annotation { "Feature Type Name" : "Feature", "Feature Type Description" : "" }
export const myFeature = defineFeature(function(context is Context, id is Id, definition is map)
    precondition{}
    {
        {
            var Q0;
            Q0=qCreatedBy(makeId("Top.planeOp"),FACE);
            var sketch = newSketch(context, id + "F0", { "sketchPlane" : qUnion([Q0])});
            skCircle(sketch, "E0", {"center": v(0.94, -3) * mm, "radius": 27.74 * mm});
            skPoint(sketch, "E0.first.point", {"position": v(1.58, 24.74) * mm});
            skPoint(sketch, "E0.second.point", {"position": v(0.52, -30.73) * mm});
            skPoint(sketch, "E0.third.point", {"position": v(-26.76, -1.33) * mm});
            skLineSegment(sketch, "E1", {"start": v(-24.87, 7.2) * mm, "end": v(-34.2, 7.2) * mm});
            skLineSegment(sketch, "E2", {"start": v(-34.2, 7.2) * mm, "end": v(-33.08, 3.11) * mm});
            skLineSegment(sketch, "E3", {"start": v(-33.08, 3.11) * mm, "end": v(-35, -2.1) * mm});
            skLineSegment(sketch, "E4", {"start": v(-35, -2.1) * mm, "end": v(-26.8, -2.1) * mm});
            skLineSegment(sketch, "E5", {"start": v(26.78, 7.1) * mm, "end": v(35.71, 7.1) * mm});
            skLineSegment(sketch, "E6", {"start": v(35.71, 7.1) * mm, "end": v(34.66, 3.21) * mm});
            skLineSegment(sketch, "E7", {"start": v(34.66, 3.21) * mm, "end": v(36.55, -2.1) * mm});
            skLineSegment(sketch, "E8", {"start": v(36.55, -2.1) * mm, "end": v(28.67, -2.25) * mm});
            skFitSpline(sketch, "E9", {"points": [v(-6, -4.72) * mm, v(-5.23, -5.35) * mm, v(-3.9, -6.35) * mm, v(-2.48, -6.98) * mm, v(-0.85, -7.35) * mm, v(0.35, -7.37) * mm, v(2.08, -7.15) * mm, v(3.86, -6.6) * mm, v(5.5, -5.84) * mm, v(6.83, -5.05) * mm, v(7.95, -4.34) * mm, v(8.2, -4.17) * mm, v(8.54, -3.89) * mm, v(8.14, -4.78) * mm, v(7.2, -5.82) * mm, v(5.2, -7.28) * mm, v(2.9, -8.45) * mm, v(3.98, -8.47) * mm, v(5.87, -8.12) * mm, v(7.76, -7.26) * mm, v(8.43, -6.75) * mm, v(8.6, -6.46) * mm, v(8.47, -7.15) * mm, v(6.46, -8.4) * mm, v(3.8, -9.28) * mm, v(1.11, -9.42) * mm, v(-0.95, -9.06) * mm], "startDerivative": vector(22.31, -18.25) * mm, "endDerivative": vector(-43, 9.84) * mm});
            skFitSpline(sketch, "E10", {"points": [v(-6, -4.72) * mm, v(-5.19, -6.01) * mm, v(-3.81, -7.48) * mm, v(-3.02, -8.2) * mm, v(-2.26, -9.47) * mm, v(-1.53, -11.45) * mm, v(-1.17, -13.95) * mm, v(-1.2, -16.67) * mm, v(-0.95, -15.45) * mm, v(-0.68, -11.98) * mm, v(-0.91, -9.36) * mm, v(-0.95, -9.06) * mm], "startDerivative": vector(8.3, -15) * mm, "endDerivative": vector(-0.86, 6) * mm});
            skFitSpline(sketch, "E11", {"points": [v(2.34, -9.66) * mm, v(2.02, -10.62) * mm, v(1.67, -12.76) * mm, v(1.67, -14.3) * mm, v(2.06, -16.19) * mm, v(2.36, -16.95) * mm, v(1.82, -16.92) * mm, v(-0.01, -17.17) * mm, v(-1.66, -17.64) * mm, v(-3.97, -18.79) * mm, v(-6.02, -20.44) * mm, v(-6.96, -21.68) * mm, v(-5.91, -20.77) * mm, v(-3.67, -19.33) * mm, v(-1.3, -18.4) * mm, v(0.83, -18.07) * mm, v(2.42, -18.3) * mm, v(3.7, -19.03) * mm, v(4.04, -19.68) * mm, v(3.45, -20.21) * mm, v(1.98, -19.81) * mm, v(1.3, -18.87) * mm, v(1.45, -19.8) * mm, v(2.36, -20.56) * mm, v(3.3, -21.02) * mm, v(4.84, -20.7) * mm, v(5.53, -19.8) * mm, v(6.38, -20.28) * mm, v(7.16, -20.84) * mm, v(8.14, -21.87) * mm, v(7.64, -20.68) * mm, v(6.28, -19.14) * mm, v(4.5, -17.53) * mm, v(3.33, -16.29) * mm, v(2.56, -14.18) * mm, v(2.24, -11.68) * mm, v(2.33, -10.24) * mm, v(2.34, -9.66) * mm]});
            skLineSegment(sketch, "E12", {"start": v(-24.87, 7.2) * mm, "end": v(28.1, 7.1) * mm});
            skLineSegment(sketch, "E13", {"start": v(-27.68, -2.1) * mm, "end": v(29.48, -2.24) * mm});
            skCircle(sketch, "E14.0", {"center": v(0.94, -3) * mm, "radius": 29.33 * mm});
            skCircle(sketch, "E15.0", {"center": v(0.94, -3) * mm, "radius": 31.31 * mm});
            skLineSegment(sketch, "E16.0", {"start": v(-24.87, 6.45) * mm, "end": v(28.1, 6.35) * mm});
            skLineSegment(sketch, "E17.0", {"start": v(-24.87, 6.45) * mm, "end": v(-33.21, 6.45) * mm});
            skLineSegment(sketch, "E18", {"start": v(28.1, 6.35) * mm, "end": v(34.73, 6.35) * mm});
            skLineSegment(sketch, "E19.0", {"start": v(-27.68, -1.35) * mm, "end": v(29.48, -1.49) * mm});
            skLineSegment(sketch, "E20", {"start": v(-27.68, -1.35) * mm, "end": v(-33.91, -1.33) * mm});
            skLineSegment(sketch, "E21", {"start": v(29.48, -1.49) * mm, "end": v(35.54, -1.5) * mm});
            skLineSegment(sketch, "E22.0", {"start": v(34.73, 6.35) * mm, "end": v(33.88, 3.18) * mm});
            skLineSegment(sketch, "E23.0", {"start": v(33.88, 3.18) * mm, "end": v(35.54, -1.5) * mm});
            skLineSegment(sketch, "E24.0", {"start": v(-32.3, 3.08) * mm, "end": v(-33.91, -1.33) * mm});
            skLineSegment(sketch, "E25.trimOffspring", {"start": v(-33.21, 6.45) * mm, "end": v(-32.3, 3.08) * mm});
            skText(sketch, "E26", { "text": "SCIENCE CHALLENGE", "fontName": "OpenSans-Regular.ttf"});
            skText(sketch, "E27", { "text": "GEMINI", "fontName": "OpenSans-Bold.ttf"});
            skText(sketch, "E28", { "text": "VJC", "fontName": "Arimo-Bold.ttf"});
            skLineSegment(sketch, "E29", {"start": v(6.9, 1.33) * mm, "end": v(6.9, 2.22) * mm});
            skLineSegment(sketch, "E30", {"start": v(6.9, 2.22) * mm, "end": v(7.18, 2.22) * mm});
            skLineSegment(sketch, "E31", {"start": v(7.18, 2.22) * mm, "end": v(7.26, 2.22) * mm});
            skLineSegment(sketch, "E32", {"start": v(7.26, 2.22) * mm, "end": v(7.26, 1.34) * mm});
            skLineSegment(sketch, "E33", {"start": v(7.26, 1.34) * mm, "end": v(6.9, 1.33) * mm});
            skCircle(sketch, "E34", {"center": v(1.48, 31.52) * mm, "radius": 3.06 * mm});
            skCircle(sketch, "E35.0", {"center": v(1.48, 31.52) * mm, "radius": 5 * mm});
            skText(sketch, "E36", { "text": "Ad Hoc", "fontName": "AllertaStencil-Regular.ttf"});
            const initialGuessF0  = {"E26": [-0.03136, 0, 1, 0, 0.0047], "E27": [-0.0116, -0.02738, 1, 0, 0.00494], "E28": [-0.01032, 0.01442, 1, 0, 0.00826], "E36": [-0.01374, 0.00786, 1, 0, 0.00598]};
            skSetInitialGuess(sketch, initialGuessF0);
            skSolve(sketch);
        }
        {
            var Q0;
            Q0=makeQuery(id+"F0.imprint","IMPRINT",FACE,{"disambiguationData":[TD([[makeQuery(id+"F0.imprint","IMPRINT",EDGE,{"derivedFrom":sQuery(id+"F0.wireOp",EDGE,"f2c7ee9f-897c-4c1d-89b3-a48ac7c6bfa7.sketch_text.stroke-0")}),1.0]])]});
            var Q1;
            {var subQ0=sQuery(id+"F0.wireOp",EDGE,"E15.0");var subQ1=sQuery(id+"F0.wireOp",EDGE,"E1");var subQ2=makeQuery(id+"F0.imprint","INTERSECT",VERTEX,{"derivedFrom":[subQ1,subQ0]});Q1=makeQuery(id+"F0.imprint","IMPRINT",FACE,{"disambiguationData":[TD([[makeQuery(id+"F0.imprint","IMPRINT",EDGE,{"disambiguationData":[TD([[subQ2,1.0]])],"derivedFrom":subQ1}),-1.0]])]});}
            var Q2;
            Q2=makeQuery(id+"F0.imprint","IMPRINT",FACE,{"disambiguationData":[TD([[makeQuery(id+"F0.imprint","IMPRINT",EDGE,{"derivedFrom":sQuery(id+"F0.wireOp",EDGE,"26462852-2f77-49b2-9a3d-6dfd93b606f1.sketch_text.stroke-0")}),1.0]])]});
            var Q3;
            {var subQ0=sQuery(id+"F0.wireOp",EDGE,"E15.0");var subQ1=sQuery(id+"F0.wireOp",EDGE,"E4");var subQ2=makeQuery(id+"F0.imprint","INTERSECT",VERTEX,{"derivedFrom":[subQ1,subQ0]});Q3=makeQuery(id+"F0.imprint","IMPRINT",FACE,{"disambiguationData":[TD([[makeQuery(id+"F0.imprint","IMPRINT",EDGE,{"disambiguationData":[TD([[subQ2,-1.0]])],"derivedFrom":subQ1}),-1.0]])]});}
            var Q4;
            {var subQ7=sQuery(id+"F0.wireOp",EDGE,"E2");Q4=makeQuery(id+"F0.imprint","IMPRINT",FACE,{"disambiguationData":[TD([[makeQuery(id+"F0.imprint","IMPRINT",EDGE,{"derivedFrom":subQ7}),1.0]])]});}
            var Q5;
            {var subQ3=sQuery(id+"F0.wireOp",EDGE,"E17.0");var subQ10=makeQuery(id+"F0.imprint","IMPRINT",VERTEX,{"derivedFrom":subQ3});Q5=makeQuery(id+"F0.imprint","IMPRINT",FACE,{"disambiguationData":[TD([[makeQuery(id+"F0.imprint","IMPRINT",EDGE,{"disambiguationData":[TD([[subQ10,1.0]])],"derivedFrom":subQ3}),-1.0]])]});}
            var Q6;
            {var subQ0=sQuery(id+"F0.wireOp",EDGE,"E1");var subQ5=sQuery(id+"F0.wireOp",EDGE,"E14.0");var subQ6=makeQuery(id+"F0.imprint","INTERSECT",VERTEX,{"derivedFrom":[subQ0,subQ5]});Q6=makeQuery(id+"F0.imprint","IMPRINT",FACE,{"disambiguationData":[TD([[makeQuery(id+"F0.imprint","IMPRINT",EDGE,{"disambiguationData":[TD([[subQ6,-1.0]])],"derivedFrom":subQ5}),1.0]])]});}
            var Q7;
            {var subQ1=sQuery(id+"F0.wireOp",EDGE,"E5");var subQ6=sQuery(id+"F0.wireOp",EDGE,"E0");var subQ7=makeQuery(id+"F0.imprint","INTERSECT",VERTEX,{"derivedFrom":[subQ6,subQ1]});Q7=makeQuery(id+"F0.imprint","IMPRINT",FACE,{"disambiguationData":[TD([[makeQuery(id+"F0.imprint","IMPRINT",EDGE,{"disambiguationData":[TD([[subQ7,1.0]])],"derivedFrom":subQ6}),-1.0]])]});}
            var Q8;
            {var subQ0=sQuery(id+"F0.wireOp",EDGE,"E15.0");var subQ1=sQuery(id+"F0.wireOp",EDGE,"E5");var subQ2=makeQuery(id+"F0.imprint","INTERSECT",VERTEX,{"derivedFrom":[subQ1,subQ0]});Q8=makeQuery(id+"F0.imprint","IMPRINT",FACE,{"disambiguationData":[TD([[makeQuery(id+"F0.imprint","IMPRINT",EDGE,{"disambiguationData":[TD([[subQ2,1.0]])],"derivedFrom":subQ1}),-1.0]])]});}
            var Q9;
            {var subQ11=sQuery(id+"F0.wireOp",EDGE,"E6");Q9=makeQuery(id+"F0.imprint","IMPRINT",FACE,{"disambiguationData":[TD([[makeQuery(id+"F0.imprint","IMPRINT",EDGE,{"derivedFrom":subQ11}),-1.0]])]});}
            var Q10;
            {var subQ0=sQuery(id+"F0.wireOp",EDGE,"E13");var subQ1=sQuery(id+"F0.wireOp",EDGE,"E0");var subQ2=makeQuery(id+"F0.imprint","INTERSECT",VERTEX,{"disambiguationData":[OD(0.0)],"derivedFrom":[subQ1,subQ0]});Q10=makeQuery(id+"F0.imprint","IMPRINT",FACE,{"disambiguationData":[TD([[makeQuery(id+"F0.imprint","IMPRINT",EDGE,{"disambiguationData":[TD([[subQ2,-1.0]])],"derivedFrom":subQ1}),1.0]])]});}
            var Q11;
            {var subQ0=sQuery(id+"F0.wireOp",EDGE,"E13");var subQ3=sQuery(id+"F0.wireOp",EDGE,"E0");var subQ4=makeQuery(id+"F0.imprint","INTERSECT",VERTEX,{"disambiguationData":[OD(0.0)],"derivedFrom":[subQ3,subQ0]});Q11=makeQuery(id+"F0.imprint","IMPRINT",FACE,{"disambiguationData":[TD([[makeQuery(id+"F0.imprint","IMPRINT",EDGE,{"disambiguationData":[TD([[subQ4,-1.0]])],"derivedFrom":subQ3}),-1.0]])]});}
            var Q12;
            {var subQ0=sQuery(id+"F0.wireOp",EDGE,"E15.0");var subQ1=sQuery(id+"F0.wireOp",EDGE,"E8");var subQ2=makeQuery(id+"F0.imprint","INTERSECT",VERTEX,{"derivedFrom":[subQ1,subQ0]});Q12=makeQuery(id+"F0.imprint","IMPRINT",FACE,{"disambiguationData":[TD([[makeQuery(id+"F0.imprint","IMPRINT",EDGE,{"disambiguationData":[TD([[subQ2,-1.0]])],"derivedFrom":subQ1}),-1.0]])]});}
            var Q13;
            {var subQ0=sQuery(id+"F0.wireOp",EDGE,"E15.0");var subQ1=sQuery(id+"F0.wireOp",EDGE,"E1");var subQ2=makeQuery(id+"F0.imprint","INTERSECT",VERTEX,{"derivedFrom":[subQ1,subQ0]});Q13=makeQuery(id+"F0.imprint","IMPRINT",FACE,{"disambiguationData":[TD([[makeQuery(id+"F0.imprint","IMPRINT",EDGE,{"disambiguationData":[TD([[subQ2,1.0]])],"derivedFrom":subQ1}),1.0]])]});}
            var Q14;
            {var subQ0=sQuery(id+"F0.wireOp",EDGE,"E15.0");var subQ1=sQuery(id+"F0.wireOp",EDGE,"E4");var subQ2=makeQuery(id+"F0.imprint","INTERSECT",VERTEX,{"derivedFrom":[subQ1,subQ0]});Q14=makeQuery(id+"F0.imprint","IMPRINT",FACE,{"disambiguationData":[TD([[makeQuery(id+"F0.imprint","IMPRINT",EDGE,{"disambiguationData":[TD([[subQ2,-1.0]])],"derivedFrom":subQ1}),1.0]])]});}
            var Q15;
            {var subQ0=sQuery(id+"F0.wireOp",EDGE,"E4");var subQ1=sQuery(id+"F0.wireOp",EDGE,"E0");var subQ2=makeQuery(id+"F0.imprint","INTERSECT",VERTEX,{"derivedFrom":[subQ1,subQ0]});Q15=makeQuery(id+"F0.imprint","IMPRINT",FACE,{"disambiguationData":[TD([[makeQuery(id+"F0.imprint","IMPRINT",EDGE,{"disambiguationData":[TD([[subQ2,1.0]])],"derivedFrom":subQ1}),-1.0]])]});}
            var Q16;
            Q16=makeQuery(id+"F0.imprint","IMPRINT",FACE,{"disambiguationData":[TD([[makeQuery(id+"F0.imprint","IMPRINT",EDGE,{"derivedFrom":sQuery(id+"F0.wireOp",EDGE,"E9")}),1.0]])]});
            var Q17;
            {var subQ0=sQuery(id+"F0.wireOp",EDGE,"E35.0");var subQ1=sQuery(id+"F0.wireOp",EDGE,"E15.0");var subQ2=makeQuery(id+"F0.imprint","INTERSECT",VERTEX,{"disambiguationData":[OD(0.0)],"derivedFrom":[subQ1,subQ0]});Q17=makeQuery(id+"F0.imprint","IMPRINT",FACE,{"disambiguationData":[TD([[makeQuery(id+"F0.imprint","IMPRINT",EDGE,{"disambiguationData":[TD([[subQ2,-1.0]])],"derivedFrom":subQ1}),-1.0]])]});}
            var Q18;
            {var subQ0=sQuery(id+"F0.wireOp",EDGE,"E35.0");var subQ1=sQuery(id+"F0.wireOp",EDGE,"E15.0");var subQ2=makeQuery(id+"F0.imprint","INTERSECT",VERTEX,{"disambiguationData":[OD(0.0)],"derivedFrom":[subQ1,subQ0]});Q18=makeQuery(id+"F0.imprint","IMPRINT",FACE,{"disambiguationData":[TD([[makeQuery(id+"F0.imprint","IMPRINT",EDGE,{"disambiguationData":[TD([[subQ2,-1.0]])],"derivedFrom":subQ1}),1.0]])]});}
            var Q19;
            Q19=makeQuery(id+"F0.imprint","IMPRINT",FACE,{"disambiguationData":[TD([[makeQuery(id+"F0.imprint","IMPRINT",EDGE,{"derivedFrom":sQuery(id+"F0.wireOp",EDGE,"E28.sketch_text.stroke-0")}),1.0]])]});
            extrude(context, id + "F1", {"entities" : qUnion([Q0, Q1, Q2, Q3, Q4, Q5, Q6, Q7, Q8, Q9, Q10, Q11, Q12, Q13, Q14, Q15, Q16, Q17, Q18, Q19]), "depth" : 6 * mm});
        }
        {
            var Q0;
            {var subQ0=sQuery(id+"F0.wireOp",EDGE,"E24.0");Q0=makeQuery(id+"F0.imprint","IMPRINT",FACE,{"disambiguationData":[TD([[makeQuery(id+"F0.imprint","IMPRINT",EDGE,{"derivedFrom":subQ0}),1.0]])]});}
            var Q1;
            {var subQ11=sQuery(id+"F0.wireOp",EDGE,"E26.sketch_text.stroke-16");Q1=makeQuery(id+"F0.imprint","IMPRINT",FACE,{"disambiguationData":[TD([[makeQuery(id+"F0.imprint","IMPRINT",EDGE,{"derivedFrom":subQ11}),1.0]])]});}
            var Q2;
            {var subQ0=sQuery(id+"F0.wireOp",EDGE,"E26.sketch_text.stroke-33");Q2=makeQuery(id+"F0.imprint","IMPRINT",FACE,{"disambiguationData":[TD([[makeQuery(id+"F0.imprint","IMPRINT",EDGE,{"derivedFrom":subQ0}),1.0]])]});}
            var Q3;
            {var subQ10=sQuery(id+"F0.wireOp",EDGE,"E26.sketch_text.stroke-28");Q3=makeQuery(id+"F0.imprint","IMPRINT",FACE,{"disambiguationData":[TD([[makeQuery(id+"F0.imprint","IMPRINT",EDGE,{"derivedFrom":subQ10}),1.0]])]});}
            var Q4;
            {var subQ25=sQuery(id+"F0.wireOp",EDGE,"E26.sketch_text.stroke-178");Q4=makeQuery(id+"F0.imprint","IMPRINT",FACE,{"disambiguationData":[TD([[makeQuery(id+"F0.imprint","IMPRINT",EDGE,{"derivedFrom":subQ25}),1.0]])]});}
            var Q5;
            {var subQ1=sQuery(id+"F0.wireOp",EDGE,"E26.sketch_text.stroke-198");var subQ3=sQuery(id+"F0.wireOp",EDGE,"E14.0");var subQ4=makeQuery(id+"F0.imprint","INTERSECT",VERTEX,{"derivedFrom":[subQ3,subQ1]});Q5=makeQuery(id+"F0.imprint","IMPRINT",FACE,{"disambiguationData":[TD([[makeQuery(id+"F0.imprint","IMPRINT",EDGE,{"disambiguationData":[TD([[subQ4,-1.0]])],"derivedFrom":subQ3}),-1.0]])]});}
            var Q6;
            {var subQ8=sQuery(id+"F0.wireOp",EDGE,"E22.0");Q6=makeQuery(id+"F0.imprint","IMPRINT",FACE,{"disambiguationData":[TD([[makeQuery(id+"F0.imprint","IMPRINT",EDGE,{"derivedFrom":subQ8}),-1.0]])]});}
            var Q7;
            {var subQ0=sQuery(id+"F0.wireOp",EDGE,"E26.sketch_text.stroke-6");Q7=makeQuery(id+"F0.imprint","IMPRINT",FACE,{"disambiguationData":[TD([[makeQuery(id+"F0.imprint","IMPRINT",EDGE,{"derivedFrom":subQ0}),1.0]])]});}
            var Q8;
            {var subQ6=sQuery(id+"F0.wireOp",EDGE,"E26.sketch_text.stroke-1");Q8=makeQuery(id+"F0.imprint","IMPRINT",FACE,{"disambiguationData":[TD([[makeQuery(id+"F0.imprint","IMPRINT",EDGE,{"derivedFrom":subQ6}),1.0]])]});}
            var Q9;
            {var subQ6=sQuery(id+"F0.wireOp",EDGE,"E26.sketch_text.stroke-189");Q9=makeQuery(id+"F0.imprint","IMPRINT",FACE,{"disambiguationData":[TD([[makeQuery(id+"F0.imprint","IMPRINT",EDGE,{"derivedFrom":subQ6}),1.0]])]});}
            var Q10;
            {var subQ5=sQuery(id+"F0.wireOp",EDGE,"E26.sketch_text.stroke-202");Q10=makeQuery(id+"F0.imprint","IMPRINT",FACE,{"disambiguationData":[TD([[makeQuery(id+"F0.imprint","IMPRINT",EDGE,{"derivedFrom":subQ5}),1.0]])]});}
            var Q11;
            {var subQ5=sQuery(id+"F0.wireOp",EDGE,"E26.sketch_text.stroke-206");Q11=makeQuery(id+"F0.imprint","IMPRINT",FACE,{"disambiguationData":[TD([[makeQuery(id+"F0.imprint","IMPRINT",EDGE,{"derivedFrom":subQ5}),1.0]])]});}
            var Q12;
            {var subQ0=sQuery(id+"F0.wireOp",EDGE,"E21");var subQ1=sQuery(id+"F0.wireOp",EDGE,"E14.0");var subQ2=makeQuery(id+"F0.imprint","INTERSECT",VERTEX,{"derivedFrom":[subQ1,subQ0]});Q12=makeQuery(id+"F0.imprint","IMPRINT",FACE,{"disambiguationData":[TD([[makeQuery(id+"F0.imprint","IMPRINT",EDGE,{"disambiguationData":[TD([[subQ2,-1.0]])],"derivedFrom":subQ1}),-1.0]])]});}
            var Q13;
            Q13=makeQuery(id+"F0.imprint","IMPRINT",FACE,{"disambiguationData":[TD([[makeQuery(id+"F0.imprint","IMPRINT",EDGE,{"derivedFrom":sQuery(id+"F0.wireOp",EDGE,"E26.sketch_text.stroke-133")}),1.0]])]});
            var Q14;
            {var subQ5=sQuery(id+"F0.wireOp",EDGE,"E26.sketch_text.stroke-26");Q14=makeQuery(id+"F0.imprint","IMPRINT",FACE,{"disambiguationData":[TD([[makeQuery(id+"F0.imprint","IMPRINT",EDGE,{"derivedFrom":subQ5}),1.0]])]});}
            var Q15;
            {var subQ1=sQuery(id+"F0.wireOp",EDGE,"E26.sketch_text.stroke-19");Q15=makeQuery(id+"F0.imprint","IMPRINT",FACE,{"disambiguationData":[TD([[makeQuery(id+"F0.imprint","IMPRINT",EDGE,{"derivedFrom":subQ1}),1.0]])]});}
            var Q16;
            {var subQ5=sQuery(id+"F0.wireOp",EDGE,"E33");Q16=makeQuery(id+"F0.imprint","IMPRINT",FACE,{"disambiguationData":[TD([[makeQuery(id+"F0.imprint","IMPRINT",EDGE,{"derivedFrom":subQ5}),-1.0]])]});}
            var Q17;
            {var subQ0=sQuery(id+"F0.wireOp",EDGE,"E32");var subQ1=sQuery(id+"F0.wireOp",EDGE,"E26.sketch_text.stroke-126");var subQ2=makeQuery(id+"F0.imprint","INTERSECT",VERTEX,{"derivedFrom":[subQ1,subQ0]});Q17=makeQuery(id+"F0.imprint","IMPRINT",FACE,{"disambiguationData":[TD([[makeQuery(id+"F0.imprint","IMPRINT",EDGE,{"disambiguationData":[TD([[subQ2,-1.0]])],"derivedFrom":subQ1}),-1.0]])]});}
            var Q18;
            {var subQ1=sQuery(id+"F0.wireOp",EDGE,"E30");Q18=makeQuery(id+"F0.imprint","IMPRINT",FACE,{"disambiguationData":[TD([[makeQuery(id+"F0.imprint","IMPRINT",EDGE,{"derivedFrom":subQ1}),-1.0]])]});}
            extrude(context, id + "F2", {"entities" : qUnion([Q0, Q1, Q2, Q3, Q4, Q5, Q6, Q7, Q8, Q9, Q10, Q11, Q12, Q13, Q14, Q15, Q16, Q17, Q18]), "depth" : 4 * mm});
        }
    });